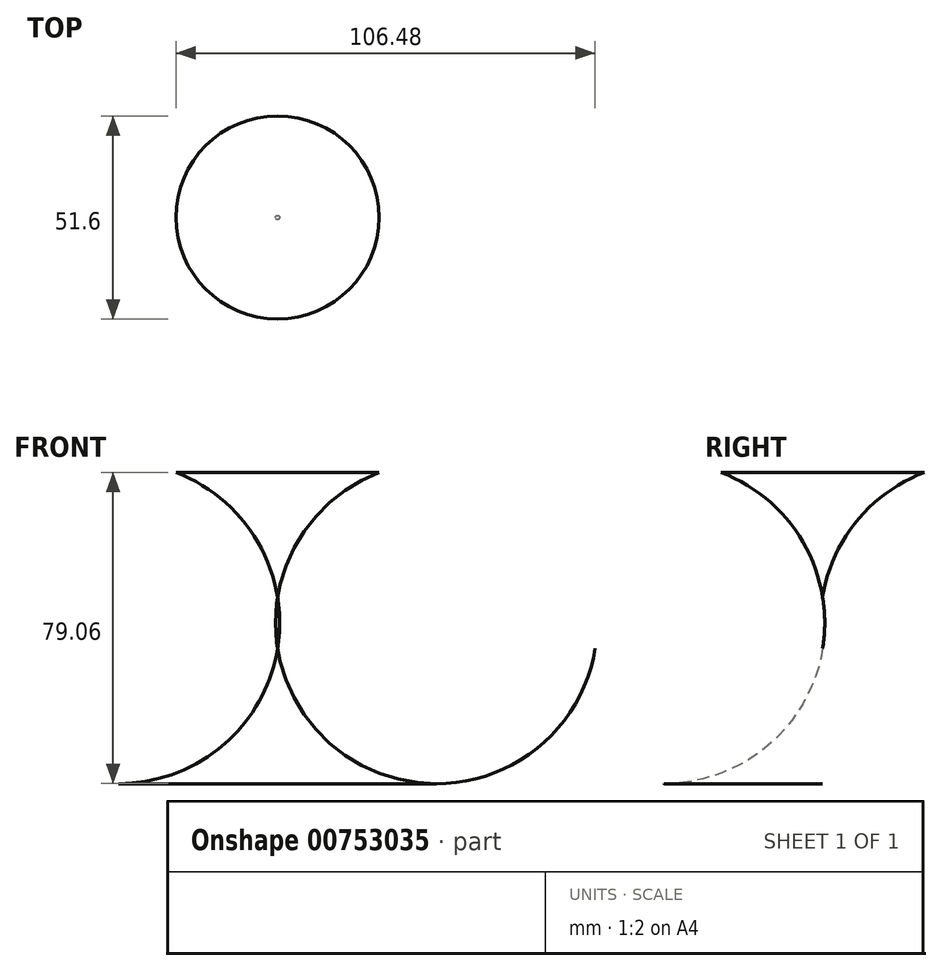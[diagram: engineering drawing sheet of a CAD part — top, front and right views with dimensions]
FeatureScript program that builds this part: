
annotation { "Feature Type Name" : "Feature", "Feature Type Description" : "" }
export const myFeature = defineFeature(function(context is Context, id is Id, definition is map)
    precondition{}
    {
        {
            var Q0;
            Q0=qCreatedBy(makeId("Front.planeOp"),FACE);
            var sketch = newSketch(context, id + "F0", { "sketchPlane" : qUnion([Q0])});
            skLineSegment(sketch, "E0", {"start": v(0, 0) * mm, "end": v(0, 73.85) * mm, "construction": true});
            skArc(sketch, "E1", {"start": v(25.8, 31.65) * mm, "mid": v(8.66, 19.28) * mm, "end": v(0, 0) * mm});
            skArc(sketch, "E2", {"start": v(0, 73.85) * mm, "mid": v(6.96, 49.12) * mm, "end": v(25.8, 31.65) * mm});
            skLineSegment(sketch, "E3", {"start": v(0, 73.85) * mm, "end": v(0, 0) * mm});
            skSolve(sketch);
        }
        {
            var Q0;
            Q0=makeQuery(id+"F0.imprint","IMPRINT",FACE,{"disambiguationData":[TD([[makeQuery(id+"F0.imprint","IMPRINT",EDGE,{"derivedFrom":sQuery(id+"F0.wireOp",EDGE,"E1")}),-1.0]])]});
            var Q1;
            Q1=sQuery(id+"F0.wireOp",EDGE,"E3");
            revolve(context, id + "F1", {"surfaceOperationType" : NewSurfaceOperationType.NEW, "entities" : qUnion([Q0]), "axis" : qUnion([Q1]), "revolveType" : RevolveType.FULL});
        }
    });
